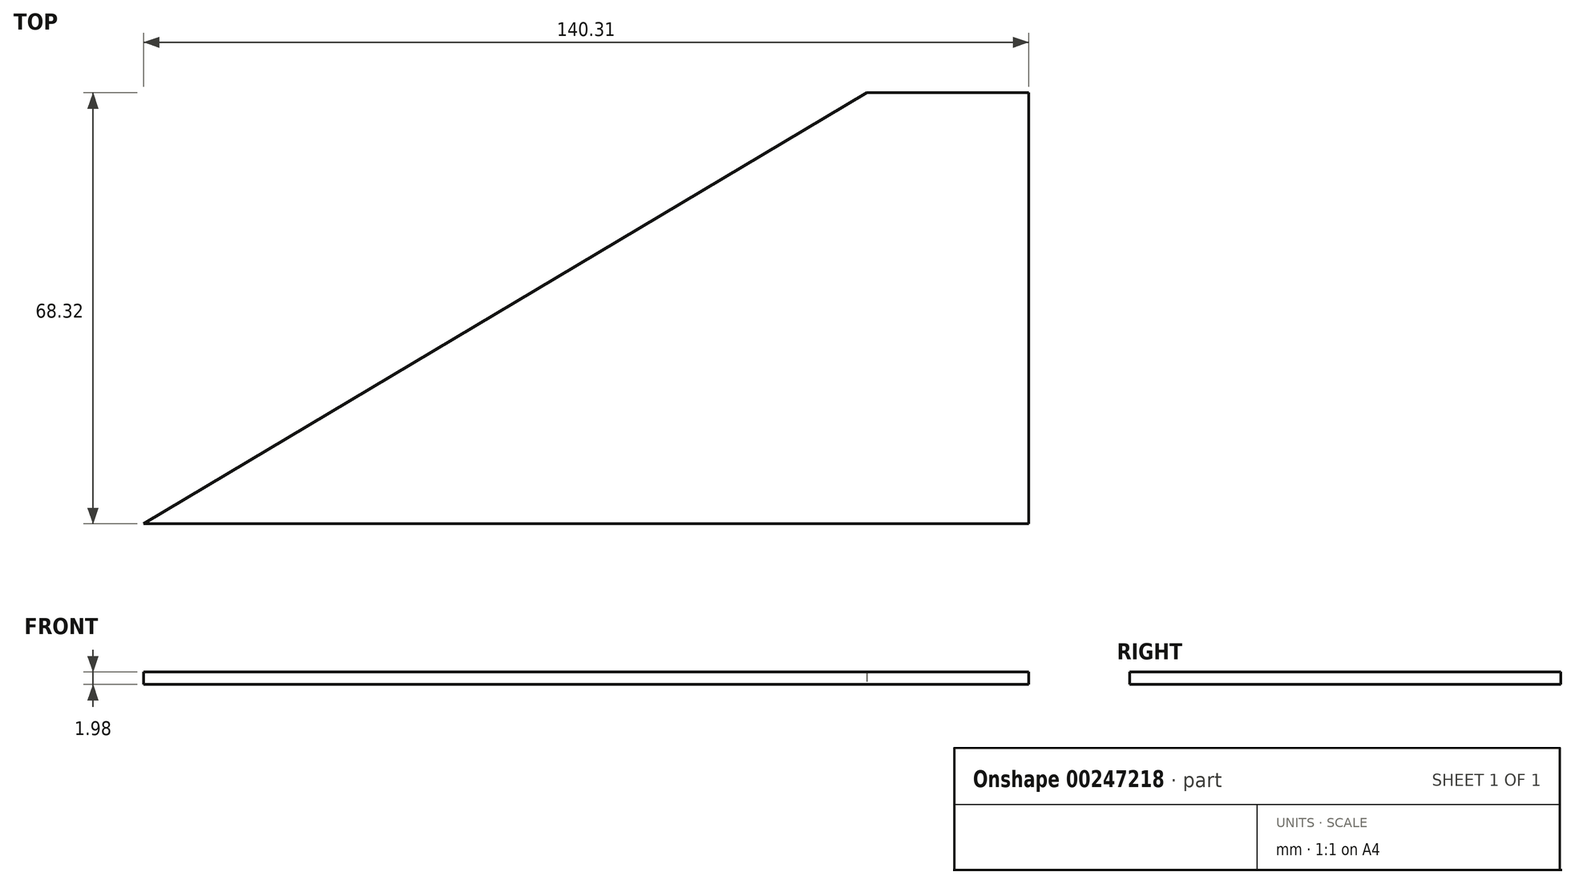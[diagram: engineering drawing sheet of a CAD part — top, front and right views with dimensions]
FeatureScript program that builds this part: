
annotation { "Feature Type Name" : "Feature", "Feature Type Description" : "" }
export const myFeature = defineFeature(function(context is Context, id is Id, definition is map)
    precondition{}
    {
        {
            var Q0;
            Q0=qCreatedBy(makeId("Top.planeOp"),FACE);
            var sketch = newSketch(context, id + "F0", { "sketchPlane" : qUnion([Q0])});
            skLineSegment(sketch, "E0", {"start": v(0, 0) * mm, "end": v(140.31, 0) * mm});
            skLineSegment(sketch, "E1", {"start": v(140.31, 68.32) * mm, "end": v(140.31, 0) * mm});
            skLineSegment(sketch, "E2", {"start": v(140.31, 68.32) * mm, "end": v(114.64, 68.32) * mm});
            skLineSegment(sketch, "E3", {"start": v(114.64, 68.32) * mm, "end": v(0, 0) * mm});
            skSolve(sketch);
        }
        {
            var Q0;
            Q0=makeQuery(id+"F0.imprint","IMPRINT",FACE,{"disambiguationData":[TD([[makeQuery(id+"F0.imprint","IMPRINT",EDGE,{"derivedFrom":sQuery(id+"F0.wireOp",EDGE,"E0")}),1.0]])]});
            extrude(context, id + "F1", {"entities" : qUnion([Q0]), "depth" : 1.98 * mm});
        }
    });
